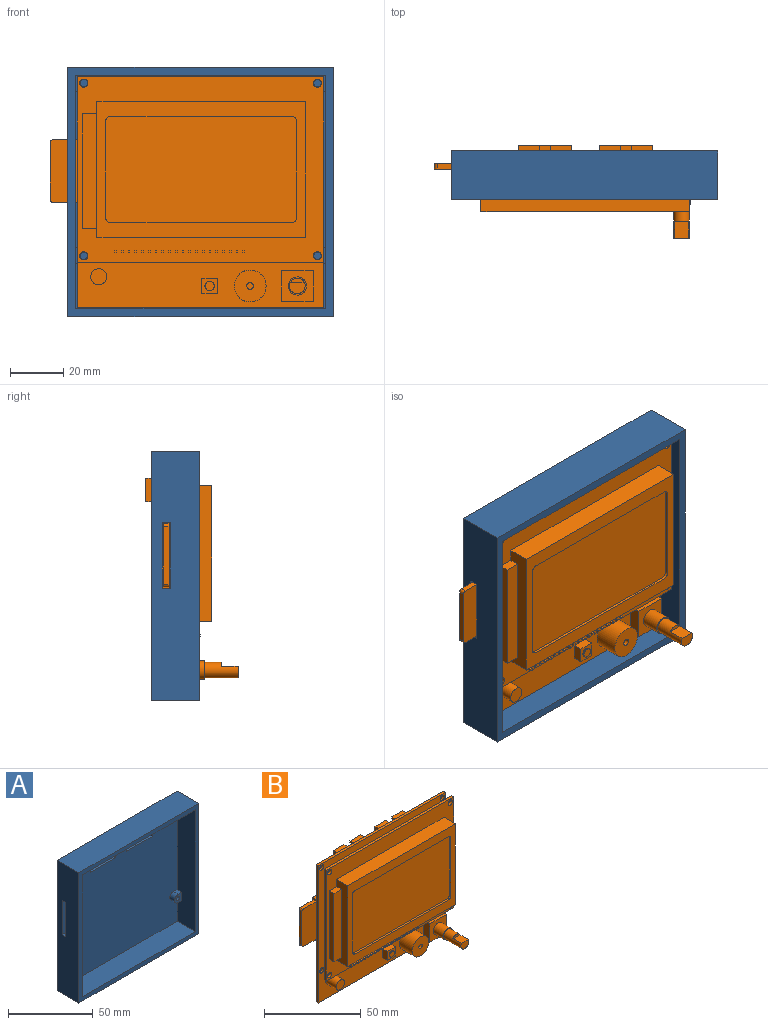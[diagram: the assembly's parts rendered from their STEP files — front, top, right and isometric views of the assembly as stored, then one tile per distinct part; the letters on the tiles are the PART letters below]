
ASSEMBLY  parts=2 mates=1
PART A: 47 faces, bbox 100x18.1x94 mm
  f0: plane 94x88mm, normal (0,-1,0), area 7719.7mm2, adj f2,f3,f9,f10,f11,f12,f14,f17
  f1: plane 100x94mm, normal (0,1,0), area 8982.4mm2, adj f5,f6,f7,f8,f39,f40,f41,f42
  f2: plane 94x15.1mm, normal (0,0,-1), area 1371mm2, adj f0,f3,f4,f10,f12,f15,f32,f33
  f3: plane 88x15.1mm, normal (1,0,0), area 1202.4mm2, adj f0,f2,f4,f9,f14,f15,f18,f20
  f4: plane 100x94mm, normal (0,-1,0), area 1128mm2, adj f2,f3,f5,f6,f7,f8,f9,f10
  f5: plane 100x18.1mm, normal (0,0,-1), area 1810mm2, adj f1,f4,f6,f7
  f6: plane 94x18.1mm, normal (1,0,0), area 1701.4mm2, adj f1,f4,f5,f8
  f7: plane 94x18.1mm, normal (-1,0,0), area 1623.4mm2, adj f1,f4,f5,f8,f35,f36,f37,f38
  f8: plane 100x18.1mm, normal (0,0,1), area 1810mm2, adj f1,f4,f6,f7
  f9: plane 94x15.1mm, normal (0,0,1), area 1419.4mm2, adj f0,f3,f4,f10
  f10: plane 88x15.1mm, normal (-1,0,0), area 1280.4mm2, adj f0,f2,f4,f9,f24,f26,f27,f30
  f11: cylinder r=3.02mm len=4mm, axis (0,1,0), area 19mm2, adj f0,f12,f14,f15
  f12: plane 4x3.03mm, normal (1,0,0), area 12.1mm2, adj f0,f2,f11,f15
  f13: cylinder r=1.4mm len=4mm, axis (0,1,0), area 35.2mm2, adj f15,f16
  f14: plane 4x3.03mm, normal (0,0,-1), area 12.1mm2, adj f0,f3,f11,f15
  f15: plane 6.05x6.05mm, normal (0,-1,0), area 28.5mm2, adj f2,f3,f11,f12,f13,f14
  f16: plane 2.8x2.8mm, normal (0,-1,0), area 6.2mm2, adj f13
  f17: cylinder r=3.02mm len=6.05mm, axis (0,1,0), area 38mm2, adj f0,f18,f20,f21
  f18: plane 4x3.03mm, normal (0,0,1), area 12.1mm2, adj f0,f3,f17,f21
  f19: cylinder r=1.4mm len=4mm, axis (0,1,0), area 35.2mm2, adj f21,f22
  f20: plane 4x3.03mm, normal (0,0,-1), area 12.1mm2, adj f0,f3,f17,f21
  f21: plane 6.05x6.05mm, normal (0,-1,0), area 26.5mm2, adj f3,f17,f18,f19,f20
  f22: plane 2.8x2.8mm, normal (0,-1,0), area 6.2mm2, adj f19
  f23: cylinder r=3.02mm len=6.05mm, axis (0,1,0), area 38mm2, adj f0,f24,f26,f27
  f24: plane 4x3.03mm, normal (0,0,-1), area 12.1mm2, adj f0,f10,f23,f27
  f25: cylinder r=1.4mm len=4mm, axis (0,1,0), area 35.2mm2, adj f27,f28
  f26: plane 4x3.03mm, normal (0,0,1), area 12.1mm2, adj f0,f10,f23,f27
  f27: plane 6.05x6.05mm, normal (0,-1,0), area 26.5mm2, adj f10,f23,f24,f25,f26
  f28: plane 2.8x2.8mm, normal (0,-1,0), area 6.2mm2, adj f25
  f29: cylinder r=3.02mm len=4mm, axis (0,1,0), area 19mm2, adj f0,f30,f32,f33
  f30: plane 4x3.03mm, normal (0,0,-1), area 12.1mm2, adj f0,f10,f29,f33
  f31: cylinder r=1.4mm len=4mm, axis (0,1,0), area 35.2mm2, adj f33,f34
  f32: plane 4x3.03mm, normal (-1,0,0), area 12.1mm2, adj f0,f2,f29,f33
  f33: plane 6.05x6.05mm, normal (0,-1,0), area 28.5mm2, adj f2,f10,f29,f30,f31,f32
  f34: plane 2.8x2.8mm, normal (0,-1,0), area 6.2mm2, adj f31
  f35: plane 24.75x3mm, normal (0,-1,0), area 74.3mm2, adj f3,f7,f36,f37
  f36: plane 3.15x3mm, normal (0,0,-1), area 9.5mm2, adj f3,f7,f35,f38
  f37: plane 3.15x3mm, normal (0,0,1), area 9.5mm2, adj f3,f7,f35,f38
  f38: plane 24.75x3mm, normal (0,1,0), area 74.3mm2, adj f3,f7,f36,f37
  f39: plane 9.85x3mm, normal (1,0,0), area 29.5mm2, adj f0,f1,f40,f42
  f40: plane 21.2x3mm, normal (0,0,-1), area 63.6mm2, adj f0,f1,f39,f41
  f41: plane 9.85x3mm, normal (-1,0,0), area 29.5mm2, adj f0,f1,f40,f42
  f42: plane 21.2x3mm, normal (0,0,1), area 63.6mm2, adj f0,f1,f39,f41
  f43: plane 21.2x3mm, normal (0,0,1), area 63.6mm2, adj f0,f1,f44,f46
  f44: plane 9.85x3mm, normal (1,0,0), area 29.5mm2, adj f0,f1,f43,f45
  f45: plane 21.2x3mm, normal (0,0,-1), area 63.6mm2, adj f0,f1,f44,f46
  f46: plane 9.85x3mm, normal (-1,0,0), area 29.5mm2, adj f0,f1,f43,f45
PART B: 206 faces, bbox 102.9x34.7x86.8 mm
  f0: plane 92.75x86.75mm, normal (0,-1,0), area 7575.7mm2, adj f6,f9,f132,f135,f136,f137,f138,f141
  f1: plane 6.83x6.83mm, normal (0,-1,0), area 9.6mm2, adj f201,f202
  f2: plane 51x8.3mm, normal (-1,0,0), area 272.8mm2, adj f3,f7,f167,f168,f169,f170,f171
  f3: plane 92.75x70mm, normal (0,-1,0), area 2221.2mm2, adj f2,f4,f7,f8,f32,f33,f34,f35
  f4: cylinder r=1.55mm len=3.1mm, axis (0,-1,0), area 15.6mm2, adj f3,f161
  f5: plane 12x11.65mm, normal (0,-1,0), area 103.2mm2, adj f141,f142,f143,f144,f201
  f6: plane 5.83x3.5mm, normal (1,0,0), area 20.4mm2, adj f0,f9,f134,f146
  f7: plane 78.45x8.3mm, normal (0,0,-1), area 651.1mm2, adj f2,f3,f166,f168
  f8: plane 43x3.5mm, normal (-1,0,0), area 150.5mm2, adj f3,f169,f170,f171
  f9: plane 5.83x3.5mm, normal (0,0,1), area 20.4mm2, adj f0,f6,f134,f145
  f10: plane 9.4x2.15mm, normal (0,0,1), area 20.2mm2, adj f26,f28,f31,f193
  f11: plane 6.9x6.45mm, normal (0,0,-1), area 44.5mm2, adj f20,f23,f181,f188
  f12: plane 9x8.85mm, normal (1,0,0), area 79.6mm2, adj f13,f15,f189,f190
  f13: plane 20.2x9mm, normal (0,0,-1), area 181.8mm2, adj f12,f14,f189,f190
  f14: plane 9x8.85mm, normal (-1,0,0), area 79.6mm2, adj f13,f15,f189,f190
  f15: plane 20.2x9mm, normal (0,0,1), area 153.4mm2, adj f12,f14,f21,f24,f25,f189,f190
  f16: plane 6.85x6.45mm, normal (-1,0,0), area 44.2mm2, adj f17,f21,f189,f192
  f17: plane 18.2x6.45mm, normal (0,0,1), area 117.4mm2, adj f16,f18,f21,f189
  f18: plane 6.85x6.45mm, normal (1,0,0), area 44.2mm2, adj f17,f19,f21,f189
  f19: plane 6.9x6.45mm, normal (0,0,-1), area 44.5mm2, adj f18,f21,f25,f189
  f20: plane 18.2x7.85mm, normal (0,1,0), area 129.1mm2, adj f11,f22,f23,f185,f186,f187,f188,f191
  f21: plane 18.2x7.85mm, normal (0,1,0), area 129.1mm2, adj f15,f16,f17,f18,f19,f24,f25,f192
  f22: plane 6.45x1mm, normal (-1,0,0), area 6.5mm2, adj f20,f181,f185,f191
  f23: plane 6.45x1mm, normal (1,0,0), area 6.5mm2, adj f11,f20,f181,f185
  f24: plane 6.45x1mm, normal (-1,0,0), area 6.5mm2, adj f15,f21,f189,f192
  f25: plane 6.45x1mm, normal (1,0,0), area 6.5mm2, adj f15,f19,f21,f189
  f26: plane 23.75x10.4mm, normal (0,1,0), area 246.6mm2, adj f10,f27,f29,f30,f31,f193
  f27: plane 9.4x2.15mm, normal (0,0,-1), area 20.2mm2, adj f26,f28,f30,f193
  f28: plane 23.75x10.4mm, normal (0,-1,0), area 246.6mm2, adj f10,f27,f29,f30,f31,f193
  f29: plane 21.75x2.15mm, normal (-1,0,0), area 46.8mm2, adj f26,f28,f30,f31
  f30: cylinder r=1mm len=2.15mm, axis (0,-1,0), area 3.4mm2, adj f26,f27,f28,f29
  f31: cylinder r=1mm len=2.15mm, axis (0,1,0), area 3.4mm2, adj f10,f26,f28,f29
  f32: plane 4x0.63mm, normal (-1,0,0), area 2.5mm2, adj f3,f33,f35,f36
  f33: plane 4x0.63mm, normal (0,0,-1), area 2.5mm2, adj f3,f32,f34,f36
  f34: plane 4x0.63mm, normal (1,0,0), area 2.5mm2, adj f3,f33,f35,f36
  f35: plane 4x0.63mm, normal (0,0,1), area 2.5mm2, adj f3,f32,f34,f36
  f36: plane 0.63x0.63mm, normal (0,-1,0), area 0.4mm2, adj f32,f33,f34,f35
  f37: plane 4x0.63mm, normal (0,0,1), area 2.5mm2, adj f3,f38,f40,f41
  f38: plane 4x0.63mm, normal (-1,0,0), area 2.5mm2, adj f3,f37,f39,f41
  f39: plane 4x0.63mm, normal (0,0,-1), area 2.5mm2, adj f3,f38,f40,f41
  f40: plane 4x0.63mm, normal (1,0,0), area 2.5mm2, adj f3,f37,f39,f41
  f41: plane 0.63x0.63mm, normal (0,-1,0), area 0.4mm2, adj f37,f38,f39,f40
  f42: plane 4x0.63mm, normal (0,0,1), area 2.5mm2, adj f3,f43,f45,f46
  f43: plane 4x0.63mm, normal (-1,0,0), area 2.5mm2, adj f3,f42,f44,f46
  f44: plane 4x0.63mm, normal (0,0,-1), area 2.5mm2, adj f3,f43,f45,f46
  f45: plane 4x0.63mm, normal (1,0,0), area 2.5mm2, adj f3,f42,f44,f46
  f46: plane 0.63x0.63mm, normal (0,-1,0), area 0.4mm2, adj f42,f43,f44,f45
  f47: plane 4x0.63mm, normal (0,0,1), area 2.5mm2, adj f3,f48,f50,f51
  f48: plane 4x0.63mm, normal (-1,0,0), area 2.5mm2, adj f3,f47,f49,f51
  f49: plane 4x0.63mm, normal (0,0,-1), area 2.5mm2, adj f3,f48,f50,f51
  f50: plane 4x0.63mm, normal (1,0,0), area 2.5mm2, adj f3,f47,f49,f51
  f51: plane 0.63x0.63mm, normal (0,-1,0), area 0.4mm2, adj f47,f48,f49,f50
  f52: plane 4x0.63mm, normal (0,0,1), area 2.5mm2, adj f3,f53,f55,f56
  f53: plane 4x0.63mm, normal (-1,0,0), area 2.5mm2, adj f3,f52,f54,f56
  f54: plane 4x0.63mm, normal (0,0,-1), area 2.5mm2, adj f3,f53,f55,f56
  f55: plane 4x0.63mm, normal (1,0,0), area 2.5mm2, adj f3,f52,f54,f56
  f56: plane 0.63x0.63mm, normal (0,-1,0), area 0.4mm2, adj f52,f53,f54,f55
  f57: plane 4x0.63mm, normal (0,0,1), area 2.5mm2, adj f3,f58,f60,f61
  f58: plane 4x0.63mm, normal (-1,0,0), area 2.5mm2, adj f3,f57,f59,f61
  f59: plane 4x0.63mm, normal (0,0,-1), area 2.5mm2, adj f3,f58,f60,f61
  f60: plane 4x0.63mm, normal (1,0,0), area 2.5mm2, adj f3,f57,f59,f61
  f61: plane 0.63x0.63mm, normal (0,-1,0), area 0.4mm2, adj f57,f58,f59,f60
  f62: plane 4x0.63mm, normal (0,0,1), area 2.5mm2, adj f3,f63,f65,f66
  f63: plane 4x0.63mm, normal (-1,0,0), area 2.5mm2, adj f3,f62,f64,f66
  f64: plane 4x0.63mm, normal (0,0,-1), area 2.5mm2, adj f3,f63,f65,f66
  f65: plane 4x0.63mm, normal (1,0,0), area 2.5mm2, adj f3,f62,f64,f66
  f66: plane 0.63x0.63mm, normal (0,-1,0), area 0.4mm2, adj f62,f63,f64,f65
  f67: plane 4x0.63mm, normal (0,0,1), area 2.5mm2, adj f3,f68,f70,f71
  f68: plane 4x0.63mm, normal (-1,0,0), area 2.5mm2, adj f3,f67,f69,f71
  f69: plane 4x0.63mm, normal (0,0,-1), area 2.5mm2, adj f3,f68,f70,f71
  f70: plane 4x0.63mm, normal (1,0,0), area 2.5mm2, adj f3,f67,f69,f71
  f71: plane 0.63x0.63mm, normal (0,-1,0), area 0.4mm2, adj f67,f68,f69,f70
  f72: plane 4x0.63mm, normal (0,0,1), area 2.5mm2, adj f3,f73,f75,f76
  f73: plane 4x0.63mm, normal (-1,0,0), area 2.5mm2, adj f3,f72,f74,f76
  f74: plane 4x0.63mm, normal (0,0,-1), area 2.5mm2, adj f3,f73,f75,f76
  f75: plane 4x0.63mm, normal (1,0,0), area 2.5mm2, adj f3,f72,f74,f76
  f76: plane 0.63x0.63mm, normal (0,-1,0), area 0.4mm2, adj f72,f73,f74,f75
  f77: plane 4x0.63mm, normal (0,0,1), area 2.5mm2, adj f3,f78,f80,f81
  f78: plane 4x0.63mm, normal (-1,0,0), area 2.5mm2, adj f3,f77,f79,f81
  f79: plane 4x0.63mm, normal (0,0,-1), area 2.5mm2, adj f3,f78,f80,f81
  f80: plane 4x0.63mm, normal (1,0,0), area 2.5mm2, adj f3,f77,f79,f81
  f81: plane 0.63x0.63mm, normal (0,-1,0), area 0.4mm2, adj f77,f78,f79,f80
  f82: plane 4x0.63mm, normal (0,0,1), area 2.5mm2, adj f3,f83,f85,f86
  f83: plane 4x0.63mm, normal (-1,0,0), area 2.5mm2, adj f3,f82,f84,f86
  f84: plane 4x0.63mm, normal (0,0,-1), area 2.5mm2, adj f3,f83,f85,f86
  f85: plane 4x0.63mm, normal (1,0,0), area 2.5mm2, adj f3,f82,f84,f86
  f86: plane 0.63x0.63mm, normal (0,-1,0), area 0.4mm2, adj f82,f83,f84,f85
  f87: plane 4x0.63mm, normal (0,0,1), area 2.5mm2, adj f3,f88,f90,f91
  f88: plane 4x0.63mm, normal (-1,0,0), area 2.5mm2, adj f3,f87,f89,f91
  f89: plane 4x0.63mm, normal (0,0,-1), area 2.5mm2, adj f3,f88,f90,f91
  f90: plane 4x0.63mm, normal (1,0,0), area 2.5mm2, adj f3,f87,f89,f91
  f91: plane 0.63x0.63mm, normal (0,-1,0), area 0.4mm2, adj f87,f88,f89,f90
  f92: plane 4x0.63mm, normal (0,0,1), area 2.5mm2, adj f3,f93,f95,f96
  f93: plane 4x0.63mm, normal (-1,0,0), area 2.5mm2, adj f3,f92,f94,f96
  f94: plane 4x0.63mm, normal (0,0,-1), area 2.5mm2, adj f3,f93,f95,f96
  f95: plane 4x0.63mm, normal (1,0,0), area 2.5mm2, adj f3,f92,f94,f96
  f96: plane 0.63x0.63mm, normal (0,-1,0), area 0.4mm2, adj f92,f93,f94,f95
  f97: plane 4x0.63mm, normal (0,0,1), area 2.5mm2, adj f3,f98,f100,f101
  f98: plane 4x0.63mm, normal (-1,0,0), area 2.5mm2, adj f3,f97,f99,f101
  f99: plane 4x0.63mm, normal (0,0,-1), area 2.5mm2, adj f3,f98,f100,f101
  f100: plane 4x0.63mm, normal (1,0,0), area 2.5mm2, adj f3,f97,f99,f101
  f101: plane 0.63x0.63mm, normal (0,-1,0), area 0.4mm2, adj f97,f98,f99,f100
  f102: plane 4x0.63mm, normal (0,0,1), area 2.5mm2, adj f3,f103,f105,f106
  f103: plane 4x0.63mm, normal (-1,0,0), area 2.5mm2, adj f3,f102,f104,f106
  f104: plane 4x0.63mm, normal (0,0,-1), area 2.5mm2, adj f3,f103,f105,f106
  f105: plane 4x0.63mm, normal (1,0,0), area 2.5mm2, adj f3,f102,f104,f106
  f106: plane 0.63x0.63mm, normal (0,-1,0), area 0.4mm2, adj f102,f103,f104,f105
  f107: plane 4x0.63mm, normal (0,0,1), area 2.5mm2, adj f3,f108,f110,f111
  f108: plane 4x0.63mm, normal (-1,0,0), area 2.5mm2, adj f3,f107,f109,f111
  f109: plane 4x0.63mm, normal (0,0,-1), area 2.5mm2, adj f3,f108,f110,f111
  f110: plane 4x0.63mm, normal (1,0,0), area 2.5mm2, adj f3,f107,f109,f111
  f111: plane 0.63x0.63mm, normal (0,-1,0), area 0.4mm2, adj f107,f108,f109,f110
  f112: plane 4x0.63mm, normal (0,0,1), area 2.5mm2, adj f3,f113,f115,f116
  f113: plane 4x0.63mm, normal (-1,0,0), area 2.5mm2, adj f3,f112,f114,f116
  f114: plane 4x0.63mm, normal (0,0,-1), area 2.5mm2, adj f3,f113,f115,f116
  f115: plane 4x0.63mm, normal (1,0,0), area 2.5mm2, adj f3,f112,f114,f116
  f116: plane 0.63x0.63mm, normal (0,-1,0), area 0.4mm2, adj f112,f113,f114,f115
  f117: plane 4x0.63mm, normal (0,0,1), area 2.5mm2, adj f3,f118,f120,f121
  f118: plane 4x0.63mm, normal (-1,0,0), area 2.5mm2, adj f3,f117,f119,f121
  f119: plane 4x0.63mm, normal (0,0,-1), area 2.5mm2, adj f3,f118,f120,f121
  f120: plane 4x0.63mm, normal (1,0,0), area 2.5mm2, adj f3,f117,f119,f121
  f121: plane 0.63x0.63mm, normal (0,-1,0), area 0.4mm2, adj f117,f118,f119,f120
  f122: plane 4x0.63mm, normal (0,0,1), area 2.5mm2, adj f3,f123,f125,f126
  f123: plane 4x0.63mm, normal (-1,0,0), area 2.5mm2, adj f3,f122,f124,f126
  f124: plane 4x0.63mm, normal (0,0,-1), area 2.5mm2, adj f3,f123,f125,f126
  f125: plane 4x0.63mm, normal (1,0,0), area 2.5mm2, adj f3,f122,f124,f126
  f126: plane 0.63x0.63mm, normal (0,-1,0), area 0.4mm2, adj f122,f123,f124,f125
  f127: plane 4x0.63mm, normal (0,0,1), area 2.5mm2, adj f3,f128,f130,f131
  f128: plane 4x0.63mm, normal (-1,0,0), area 2.5mm2, adj f3,f127,f129,f131
  f129: plane 4x0.63mm, normal (0,0,-1), area 2.5mm2, adj f3,f128,f130,f131
  f130: plane 4x0.63mm, normal (1,0,0), area 2.5mm2, adj f3,f127,f129,f131
  f131: plane 0.63x0.63mm, normal (0,-1,0), area 0.4mm2, adj f127,f128,f129,f130
  f132: cylinder r=3mm len=8mm, axis (0,-1,0), area 150.8mm2, adj f0,f133
  f133: plane 6x6mm, normal (0,-1,0), area 28.3mm2, adj f132
  f134: plane 5.83x5.83mm, normal (0,-1,0), area 24.4mm2, adj f6,f9,f145,f146,f200
  f135: plane 86.75x1.6mm, normal (-1,0,0), area 138.8mm2, adj f0,f136,f138,f190
  f136: plane 92.75x1.6mm, normal (0,0,-1), area 148.4mm2, adj f0,f135,f137,f190
  f137: plane 86.75x1.6mm, normal (1,0,0), area 138.8mm2, adj f0,f136,f138,f190
  f138: plane 92.75x1.6mm, normal (0,0,1), area 148.4mm2, adj f0,f135,f137,f190
  f139: plane 12x12mm, normal (0,-1,0), area 108.2mm2, adj f198,f199
  f140: plane 2.5x2.5mm, normal (0,-1,0), area 4.9mm2, adj f199
  f141: plane 11.65x4.5mm, normal (1,0,0), area 52.4mm2, adj f0,f5,f142,f144
  f142: plane 12x4.5mm, normal (0,0,1), area 54mm2, adj f0,f5,f141,f143
  f143: plane 11.65x4.5mm, normal (-1,0,0), area 52.4mm2, adj f0,f5,f142,f144
  f144: plane 12x4.5mm, normal (0,0,-1), area 54mm2, adj f0,f5,f141,f143
  f145: plane 5.83x3.5mm, normal (-1,0,0), area 20.4mm2, adj f0,f9,f134,f146
  f146: plane 5.83x3.5mm, normal (0,0,-1), area 20.4mm2, adj f0,f6,f134,f145
  f147: plane 3.5x3.5mm, normal (0,-1,0), area 9.6mm2, adj f200
  f148: plane 5.09x1.47mm, normal (0,-1,0), area 5.3mm2, adj f149,f202
  f149: plane 6.2x5.09mm, normal (0,0,1), area 31.5mm2, adj f148,f150,f202
  f150: plane 5.87x4.4mm, normal (0,-1,0), area 21.8mm2, adj f149,f202
  f151: plane 25.75x3mm, normal (0,0,1), area 77.2mm2, adj f152,f156,f190,f193
  f152: plane 24.4x3mm, normal (1,0,0), area 73.2mm2, adj f151,f153,f156,f190
  f153: plane 5.5x3mm, normal (0,0,-1), area 16.5mm2, adj f152,f154,f156,f190
  f154: plane 3x2mm, normal (0.71,0,-0.71), area 8.5mm2, adj f153,f155,f156,f190
  f155: plane 18.25x3mm, normal (0,0,-1), area 54.7mm2, adj f154,f156,f190,f193
  f156: plane 26.4x25.75mm, normal (0,1,0), area 666.8mm2, adj f151,f152,f153,f154,f155,f193
  f157: plane 4.2x2.5mm, normal (-1,0,0), area 10.5mm2, adj f0,f158,f160,f161
  f158: plane 50x4.2mm, normal (0,0,-1), area 210mm2, adj f0,f157,f159,f161
  f159: plane 4.2x2.5mm, normal (1,0,0), area 10.5mm2, adj f0,f158,f160,f161
  f160: plane 50x4.2mm, normal (0,0,1), area 210mm2, adj f0,f157,f159,f161
  f161: plane 92.75x70mm, normal (0,1,0), area 6337.3mm2, adj f4,f157,f158,f159,f160,f162,f163,f164
  f162: plane 70x1.6mm, normal (1,0,0), area 112mm2, adj f3,f161,f163,f165
  f163: plane 92.75x1.6mm, normal (0,0,1), area 148.4mm2, adj f3,f161,f162,f164
  f164: plane 70x1.6mm, normal (-1,0,0), area 112mm2, adj f3,f161,f163,f165
  f165: plane 92.75x1.6mm, normal (0,0,-1), area 148.4mm2, adj f3,f161,f162,f164
  f166: plane 51x8.3mm, normal (1,0,0), area 423.3mm2, adj f3,f7,f167,f168
  f167: plane 78.45x8.3mm, normal (0,0,1), area 651.1mm2, adj f2,f3,f166,f168
  f168: plane 78.45x51mm, normal (0,-1,0), area 1124.4mm2, adj f2,f7,f166,f167,f172,f173,f174,f175
  f169: plane 5.4x3.5mm, normal (0,0,1), area 18.9mm2, adj f2,f3,f8,f171
  f170: plane 5.4x3.5mm, normal (0,0,-1), area 18.9mm2, adj f2,f3,f8,f171
  f171: plane 43x5.4mm, normal (0,-1,0), area 232.2mm2, adj f2,f8,f169,f170
  f172: plane 68x1mm, normal (0,0,-1), area 68mm2, adj f168,f173,f179,f180
  f173: cylinder r=2mm len=2mm, axis (0,1,0), area 3.1mm2, adj f168,f172,f174,f180
  f174: plane 36x1mm, normal (-1,0,0), area 36mm2, adj f168,f173,f175,f180
  f175: cylinder r=2mm len=2mm, axis (0,1,0), area 3.1mm2, adj f168,f174,f176,f180
  f176: plane 68x1mm, normal (0,0,1), area 68mm2, adj f168,f175,f177,f180
  f177: cylinder r=2mm len=2mm, axis (0,1,0), area 3.1mm2, adj f168,f176,f178,f180
  f178: plane 36x1mm, normal (1,0,0), area 36mm2, adj f168,f177,f179,f180
  f179: cylinder r=2mm len=2mm, axis (0,1,0), area 3.1mm2, adj f168,f172,f178,f180
  f180: plane 72x40mm, normal (0,-1,0), area 2876.6mm2, adj f172,f173,f174,f175,f176,f177,f178,f179
  f181: plane 20.2x8.85mm, normal (0,1,0), area 49.7mm2, adj f11,f22,f23,f182,f183,f184,f185,f186
  f182: plane 9x8.85mm, normal (1,0,0), area 79.6mm2, adj f181,f183,f185,f190
  f183: plane 20.2x9mm, normal (0,0,-1), area 181.8mm2, adj f181,f182,f184,f190
  f184: plane 9x8.85mm, normal (-1,0,0), area 79.6mm2, adj f181,f183,f185,f190
  f185: plane 20.2x9mm, normal (0,0,1), area 153.4mm2, adj f20,f22,f23,f181,f182,f184,f190
  f186: plane 6.85x6.45mm, normal (-1,0,0), area 44.2mm2, adj f20,f181,f187,f191
  f187: plane 18.2x6.45mm, normal (0,0,1), area 117.4mm2, adj f20,f181,f186,f188
  f188: plane 6.85x6.45mm, normal (1,0,0), area 44.2mm2, adj f11,f20,f181,f187
  f189: plane 20.2x8.85mm, normal (0,1,0), area 49.7mm2, adj f12,f13,f14,f15,f16,f17,f18,f19
  f190: plane 92.75x86.75mm, normal (0,1,0), area 6991.5mm2, adj f12,f13,f14,f15,f135,f136,f137,f138
  f191: plane 6.9x6.45mm, normal (0,0,-1), area 44.5mm2, adj f20,f22,f181,f186
  f192: plane 6.9x6.45mm, normal (0,0,-1), area 44.5mm2, adj f16,f21,f24,f189
  f193: plane 26.4x3mm, normal (-1,0,0), area 28.1mm2, adj f10,f26,f27,f28,f151,f155,f156,f190
  f194: cylinder r=1.55mm len=3.1mm, axis (0,-1,0), area 15.6mm2, adj f0,f190
  f195: cylinder r=1.55mm len=3.1mm, axis (0,-1,0), area 15.6mm2, adj f0,f190
  f196: cylinder r=1.55mm len=3.1mm, axis (0,-1,0), area 15.6mm2, adj f0,f190
  f197: cylinder r=1.55mm len=3.1mm, axis (0,-1,0), area 15.6mm2, adj f0,f190
  f198: cylinder r=6mm len=12mm, axis (0,-1,0), area 358.1mm2, adj f0,f139
  f199: cylinder r=1.25mm len=5mm, axis (0,1,0), area 39.3mm2, adj f139,f140
  f200: cylinder r=1.75mm len=3.5mm, axis (0,-1,0), area 5.5mm2, adj f134,f147
  f201: cylinder r=3.42mm len=7mm, axis (0,-1,0), area 150.2mm2, adj f1,f5
  f202: cylinder r=2.94mm len=12.6mm, axis (0,-1,0), area 194.2mm2, adj f1,f148,f149,f150
  f203: cylinder r=1.55mm len=3.1mm, axis (0,-1,0), area 15.6mm2, adj f3,f161
  f204: cylinder r=1.55mm len=3.1mm, axis (0,-1,0), area 15.6mm2, adj f3,f161
  f205: cylinder r=1.55mm len=3.1mm, axis (0,-1,0), area 15.6mm2, adj f3,f161
PLACE A t=(0,-6.8,0)mm
PLACE B t=(0,-13.8,0)mm fixed
MATE fastened B.f197 <-> A.f17  axis (0,1,0) through (-43.98,-13.8,-24.03)mm
